# Revit family: UNB_Multisuites_E1482_BIM_NL
name_source: partatom
category: Plumbing Fixtures
units: mm (PartAtom-declared; Revit-internal decimal feet)

## family parameters
Always vertical = No
Cut with Voids When Loaded = No
OmniClass Number = 23.45.55.21
OmniClass Title = Drains (Wastes)
Part Type = Normal
Room Calculation Point = No
Round Connector Dimension = Use Diameter
Shared = No
Work Plane-Based = No

## types (5) — shared parameters
Accesoires = https://www.idealstandard.nl
Accessories = https://www.idealstandard.nl
Afmetingen = 125 x 64 x 64mm
AfstandsEenheid = Millimeter
AreaUnits = Millimetres
Artikelomschrijving = BECKENKLICK ABFALL, SCHLITZE
Artikelreferentie = BASIN CLICK WASTE , SLOTTED
Auteur = Ideal Standard
BIMObjectName = IS_IdealStandard_Showermixers_Multisuites_E1482
BIMobject category = Sanitary
BIMobject category code = Taps & Mixers
BIMobject main category = Sanitary
Beschrijvinggarantie = Herstellergarantie
BimObjectNaam = IS_IdealStandard_Showermixers_Multisuites_E1482
Brand = Ideal Standard
Brand url = http://www.idealstandard.nl
Breedte = 63.500844
ConnectionType = Installation
CurrencyUnit = €
CurrentRevision = 1
Date of publishing = 24/07/2021
Diepte = 64 mm
Douchebak = No
DurationUnit = Years
Edition number = 1
Garantieonderdelen = 5
Garantieunits = Jaren
GemaaktOp = 27/07/2021
HasIntegralShutOffDevice = No
Help = https://www.idealstandard.nl
Hoogte = 125.022602081299
Hulp = https://www.idealstandard.nl
IFC Classification = Sanitary Terminal
IfcExportAs = IfcValveType
IfcExportType = MIXING
Installatieinstructies = https://www.idealstandard.nl
Installation instructions = https://www.idealstandard.nl
InstallationInstructions = https://www.idealstandard.nl
IsBuiltIn = No
IsHighPressure = No
LinearUnits = Millimetres
MaintenanceInformation = https://www.idealstandard.nl
Manufacturer = Ideal Standard
Manufacturer name = Ideal Standard
ManufacturerURL = https://www.idealstandard.nl
Materiaal = Messing
Material = Brass
Material main = Brass
Merk = Ideal Standard
ModelReference = BASIN CLICK WASTE , SLOTTED
Montageinstuctie = https://www.idealstandard.nl
NBS Reference Code = 45-35-70/335
NBS Reference Description = Shower mixers
Name = Showermixers_Multisuites_E1482_IdealStandard
NettWeight = 0.37
Nettogewicht = 0.37
NominalDepth = 64 mm
NominalHeight = 125 mm
NominalLength = 64 mm
NominalWidth = 64 mm
Normen = Showermixers_Multisuites_E1482_IdealStandard
OppervlakteEenheid = Millimeter
Product Guid = 820e9b25-9249-4381-a1dc-fc5daed826e8
Product SKU = E1482
Product certification = https://www.idealstandard.nl
Product data url = https://bimobject.com
Product family = Sanitary
Product group = Showers
Product name = BASIN CLICK WASTE , SLOTTED
Product url = https://www.idealstandard.nl
ProductInformation = https://www.idealstandard.nl
ProductSoort = Sanitary
Productinformatie = https://www.idealstandard.nl
QR code = http://bimobject.com
Referentie = BASIN CLICK WASTE , SLOTTED
Revisie = 1
Shape = Cylindrical
Size = 125 x 64 x 64mm
Space = Internal
SpareParts = https://www.idealstandard.nl
Technical description = https://www.idealstandard.nl
Telefoonnummer = 077 355 08 08
TestPressure = 10 Bar
Testdruk = 10 Bar
Typeconnectie = Installation
URL = https://www.idealstandard.nl
Uniclass 2015 Code = Pr_40_20_87_80
Uniclass 2015 Name = Shower thermostatic valves
Uniclass2015Beschrijving = Shower thermostatic valves
Uniclass2015Code = Pr_40_20_87_80
Uniclass2015Referentie = Pr_40_20_87_80
Uniclass2015Title = Shower thermostatic valves
Uniclass2015Version = v1.22
Urlproducent = https://www.idealstandard.nl
ValutaEenheid = Euro
Versie = 1
Version = 1
VolumeUnits = Litres
Volumeunits = Liters
Vorm = zylindrisch
WRASApprovalNumber = 1810015
WRASURL = https://www.wrasapprovals.co.uk
WarrantyDescription = Manufacturer warranty
WarrantyDurationUnit = Years
Wisselstukken = https://www.idealstandard.nl
WrasExpiryDate = 31.10.2023
Youtube clip = https://www.youtube.com
zero-valued in all types: BrutoGewicht, Cost, Lengte, Vervangingskosten

## per-type parameters (varying)
| type | Afwerking | Artikelnummer | BarCode | Barcode | Color | Description | Eigenschappen | Features | Finish | GTIN code | Kleur | MainColor | Model | ModelNumber |
| E1482AA - BASIN CLICK WASTE , SLOTTED - CHROME | Chrom | E1482AA | 5017830536215 | 5017830536215 | Chrom | BECKENKLICK ABFALL, SCHLITZE - CHROM | BECKENKLICK ABFALL, SCHLITZE - CHROM | BECKENKLICK ABFALL, SCHLITZE - CHROM | Chrom | https://5017830536215 | Chrom | Chrom | E1482AA | E1482AA |
| E1482A5 - BASIN CLICK WASTE , SLOTTED - MAGNETIC GREY | magnetisch grau | E1482A5 | 5017830548805 | 5017830548805 | magnetisch grau | BECKENKLICK ABFALL, SCHLITZE - MAGNETISCHES GRAU | BECKENKLICK ABFALL, SCHLITZE - MAGNETISCHES GRAU | BECKENKLICK ABFALL, SCHLITZE - MAGNETISCHES GRAU | magnetisch grau | https://5017830548805 | magnetisch grau | magnetisch grau | E1482A5 | E1482A5 |
| E1482XG - BASIN CLICK WASTE , SLOTTED - SILK BLACK | Seide schwarz | E1482XG | 5017830552567 | 5017830552567 | Seide schwarz | BECKENKLICK ABFALL, SCHLITZE - SEIDE SCHWARZ | BECKENKLICK ABFALL, SCHLITZE - SEIDE SCHWARZ | BECKENKLICK ABFALL, SCHLITZE - SEIDE SCHWARZ | Seide schwarz | https://5017830552567 | Seide schwarz | Seide schwarz | E1482XG | E1482XG |
| E1482GN - BASIN CLICK WASTE , SLOTTED - SILVER STORM | silberner Sturm | E1482GN | 5017830548812 | 5017830548812 | silberner Sturm | BECKENKLICK ABFALL, SCHLITZE - SILBER STURM | BECKENKLICK ABFALL, SCHLITZE - SILBER STURM | BECKENKLICK ABFALL, SCHLITZE - SILBER STURM | silberner Sturm | https://5017830548812 | silberner Sturm | silberner Sturm | E1482GN | E1482GN |
| E1482A2 - BASIN CLICK WASTE , SLOTTED - BRUSH GOLD | Pinsel gold | E1482A2 | 5017830548799 | 5017830548799 | Pinsel gold | BECKENKLICK ABFALL, SCHLITZE - PINSEL GOLD | BECKENKLICK ABFALL, SCHLITZE - PINSEL GOLD | BECKENKLICK ABFALL, SCHLITZE - PINSEL GOLD | Pinsel gold | https://5017830548799 | Pinsel gold | Pinsel gold | E1482A2 | E1482A2 |

## geometry (parser evidence)
native form markers: Sweep x4
no freeform markers — native parametric forms only
